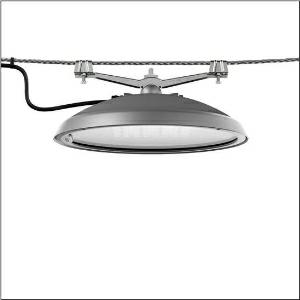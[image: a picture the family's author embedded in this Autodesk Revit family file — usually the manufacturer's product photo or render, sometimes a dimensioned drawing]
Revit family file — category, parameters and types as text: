
# Revit family: dl_r__50_iq_mini___st1_0s_5xa248w21f08he_f114
name_source: partatom
category: Lighting Fixtures
units: mm (PartAtom-declared; Revit-internal decimal feet)

## family parameters
Cut with Voids When Loaded = No
Host = Face
Light Source = No
Part Type = Normal
Room Calculation Point = No
Round Connector Dimension = Use Diameter
Shared = No

## types (1)
- --- (1 x LED, 7840 lm, 69.3 W, 2200K)
    Apparent Load = 69 VA
    CIE Flux Codes = 37 72 97 100 100
    Color Rendering = 70
    Color Temperature = 2200K
    Default Elevation = 1800 mm
    Description = DL® 50 iQ mini, catenary luminaire, primary light control with lens, of PMMA, primary optical cover: cover, of toughened safety glass, transparent, light distribution: ST1.0s, light emission: direct distribution, primary light characteristic: symmetric, installation type: suspended mounting, LED, High Power LED, rated luminous flux: 7.840lm, luminous efficacy: 113lm/W, light colour: 722, colour temperature: 2200K, control gear: iQ Street-Remote, control: optimised constant luminous flux control (CLO 2.0), Desk-Remote (wireless, voltage-free reading and setting of iQ features in the workshop via application-optimized NFC function/RFID function), Light-Fading, Smart-Wire, Night-Set, Lumen-Switch, Temp-Guard, Auto-Match, Street-Remote, mains connection: 230..240V, AC, 50/60Hz, start of lifetime: 69W, end of service life: 74W, reduction: 30W, luminaire housing, of diecast aluminium, powder-coated, Siteco® metallic grey (DB 702S), diameter: 500mm, height: 115mm, mounting height: 4..12m, protection rating (complete): IP66, insulation class (complete): insulation class II (safety insulation), certification: CE, ENEC, ENEC+, VDE, impact resistance: IK08, permissible operating ambient temperature for outdoor applications: -25..+40°C, standard-compliant lighting for roads and squares, packaging unit: 1 piece

Light Distribution: ST1.0s
    Height = 124 mm  [stored 0.406824 ft]
    Lamp = 1 x LED
    Lamp Light Flux = 7840 lm
    Lamp Power = 69.3 W
    Lamp count = 1
    Length = 500 mm
    Luminous efficacy = 113 lm/W
    Manufacturer = Siteco
    ModVariant = No
    Model = 5XA248W21F08HE
    Number of Poles = 1
    OnlyDefault = Yes
    Power Factor = 1
    Product Name = DL® 50 iQ mini | ST1.0s
    Product group = catenary luminaire
    ProductGroupID = 6300
    Protection Class = Protection class II
    Protection Degree = IP 66
    RLX_Detail_Level = 1
    RLX_Emergency_Light_Flux = 0 lm
    RLX_Emergency_Type = 0
    RLX_Emergency_Type_DB = No
    RlxData = <blob elided: 123505 chars, md5=af2183fb>
    Socket = socket
    Standby Power = 0 W
    System Light Flux = 7840 lm
    System Power = 69 W
    Type Comments = factory setting: luminous flux: 100 % | dim-lin: 254 | 700 mA
    Type Image = l_1242791.jpg
    URL = http://relux.com
    VarID = @adj_140678
    Voltage = 0 V
    Weight = 0.00 kg
    Width = 0 mm  [stored 0 ft]

note: [stored X ft] marks values corroborated as IEEE doubles in the binary element streams (Revit-internal decimal feet)

## geometry (parser evidence)
native form markers: Blend x4, Sweep x13
no freeform markers — native parametric forms only
